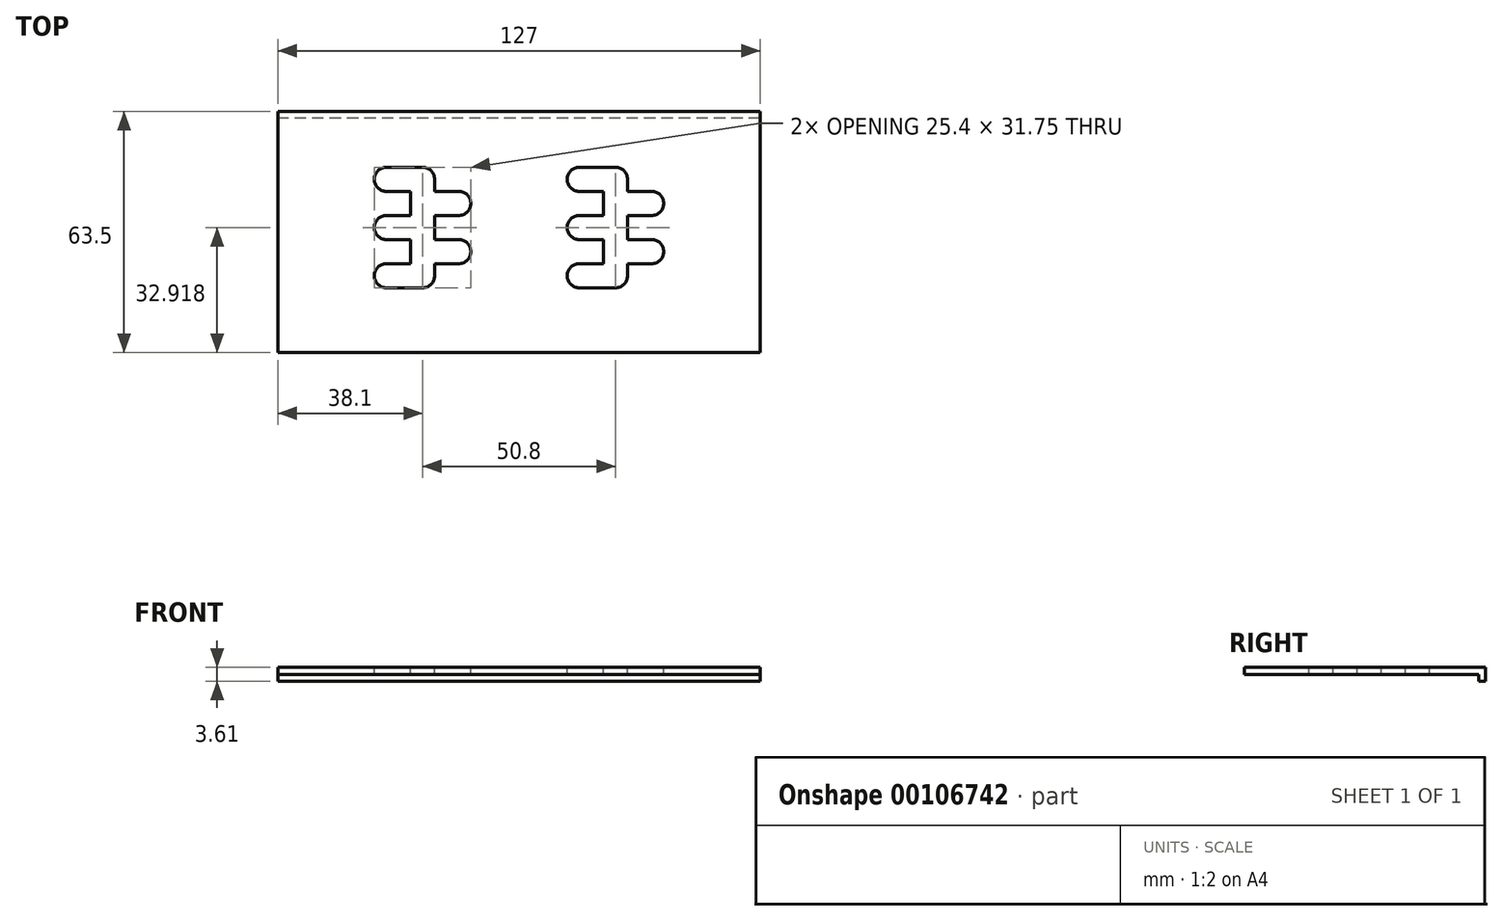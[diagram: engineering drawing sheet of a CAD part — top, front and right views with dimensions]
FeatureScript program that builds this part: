
annotation { "Feature Type Name" : "Feature", "Feature Type Description" : "" }
export const myFeature = defineFeature(function(context is Context, id is Id, definition is map)
    precondition{}
    {
        {
            var Q0;
            Q0=qCreatedBy(makeId("Right.planeOp"),FACE);
            var sketch = newSketch(context, id + "F0", { "sketchPlane" : qUnion([Q0])});
            skLineSegment(sketch, "E0.bottom", {"start": v(29.95, -0.9) * mm, "end": v(-31.75, -0.9) * mm});
            skLineSegment(sketch, "E0.top", {"start": v(31.75, 0.9) * mm, "end": v(-31.75, 0.9) * mm});
            skLineSegment(sketch, "E0.left", {"start": v(31.75, -0.9) * mm, "end": v(31.75, 0.9) * mm});
            skLineSegment(sketch, "E0.right", {"start": v(-31.75, -0.9) * mm, "end": v(-31.75, 0.9) * mm});
            skPoint(sketch, "E0.middle", {"position": v(0, 0) * mm});
            skLineSegment(sketch, "E1", {"start": v(31.75, -0.9) * mm, "end": v(31.75, -2.7) * mm});
            skLineSegment(sketch, "E2", {"start": v(31.75, -2.7) * mm, "end": v(29.95, -2.7) * mm});
            skLineSegment(sketch, "E3", {"start": v(29.95, -2.7) * mm, "end": v(29.95, -0.9) * mm});
            skSolve(sketch);
        }
        {
            var Q0;
            Q0=makeQuery(id+"F0.imprint","IMPRINT",FACE,{"disambiguationData":[TD([[makeQuery(id+"F0.imprint","IMPRINT",EDGE,{"derivedFrom":sQuery(id+"F0.wireOp",EDGE,"E0.bottom")}),-1.0]])]});
            extrude(context, id + "F1", {"entities" : qUnion([Q0]), "depth" : 63.5 * mm, "hasSecondDirection" : true, "secondDirectionOppositeDirection" : true, "secondDirectionDepth" : 63.5 * mm});
        }
        {
            var Q0;
            Q0=makeQuery(id+"F1.opExtrude","SWEPT_FACE",FACE,{"disambiguationData":[OSD([sQuery(id+"F0.wireOp",EDGE,"E0.top")])]});
            var sketch = newSketch(context, id + "F2", { "sketchPlane" : qUnion([Q0])});
            skLineSegment(sketch, "E4", {"start": v(0, 0) * mm, "end": v(-25.4, 0) * mm, "construction": true});
            skLineSegment(sketch, "E5", {"start": v(-38.1, 13.87) * mm, "end": v(-25.4, 13.87) * mm, "construction": true});
            skLineSegment(sketch, "E6", {"start": v(-25.4, 13.87) * mm, "end": v(-25.4, -11.53) * mm, "construction": true});
            skLineSegment(sketch, "E7", {"start": v(-38.1, -11.53) * mm, "end": v(-25.4, -11.53) * mm, "construction": true});
            skLineSegment(sketch, "E8", {"start": v(-25.4, 1.17) * mm, "end": v(-38.1, 1.17) * mm, "construction": true});
            skLineSegment(sketch, "E9", {"start": v(-25.4, 7.52) * mm, "end": v(-12.7, 7.52) * mm, "construction": true});
            skLineSegment(sketch, "E10", {"start": v(-25.4, -5.18) * mm, "end": v(-12.7, -5.18) * mm, "construction": true});
            skLineSegment(sketch, "E11", {"start": v(-38.1, 13.87) * mm, "end": v(-38.1, 13.87) * mm});
            skLineSegment(sketch, "E12", {"start": v(-34.93, 17.04) * mm, "end": v(-25.4, 17.04) * mm});
            skLineSegment(sketch, "E13", {"start": v(-12.7, 7.52) * mm, "end": v(-12.7, 7.52) * mm});
            skLineSegment(sketch, "E14", {"start": v(-22.23, 13.87) * mm, "end": v(-22.23, 10.7) * mm});
            skLineSegment(sketch, "E15", {"start": v(-15.88, 10.7) * mm, "end": v(-22.23, 10.7) * mm});
            skLineSegment(sketch, "E16", {"start": v(-15.88, 4.34) * mm, "end": v(-22.23, 4.34) * mm});
            skLineSegment(sketch, "E17", {"start": v(-22.23, 4.34) * mm, "end": v(-22.23, -2) * mm});
            skLineSegment(sketch, "E18", {"start": v(-12.7, -5.18) * mm, "end": v(-12.7, -5.18) * mm});
            skLineSegment(sketch, "E19", {"start": v(-15.88, -2) * mm, "end": v(-22.23, -2) * mm});
            skLineSegment(sketch, "E20", {"start": v(-15.88, -8.36) * mm, "end": v(-22.23, -8.36) * mm});
            skLineSegment(sketch, "E21", {"start": v(-22.23, -8.36) * mm, "end": v(-22.23, -11.53) * mm});
            skLineSegment(sketch, "E22", {"start": v(-25.4, -14.7) * mm, "end": v(-34.93, -14.7) * mm});
            skLineSegment(sketch, "E23", {"start": v(-38.1, -11.53) * mm, "end": v(-38.1, -11.53) * mm});
            skLineSegment(sketch, "E24", {"start": v(-34.93, -8.36) * mm, "end": v(-28.58, -8.36) * mm});
            skLineSegment(sketch, "E25", {"start": v(-28.58, -8.36) * mm, "end": v(-28.58, -2) * mm});
            skLineSegment(sketch, "E26", {"start": v(-28.58, -2) * mm, "end": v(-34.93, -2) * mm});
            skLineSegment(sketch, "E27", {"start": v(-38.1, 1.17) * mm, "end": v(-38.1, 1.17) * mm});
            skLineSegment(sketch, "E28", {"start": v(-34.93, 10.7) * mm, "end": v(-28.58, 10.7) * mm});
            skLineSegment(sketch, "E29", {"start": v(-28.58, 10.7) * mm, "end": v(-28.58, 4.34) * mm});
            skLineSegment(sketch, "E30", {"start": v(-28.58, 4.34) * mm, "end": v(-34.93, 4.34) * mm});
            skPoint(sketch, "E31.visualSharp", {"position": v(-38.1, 17.04) * mm});
            skArc(sketch, "E31.filletArc", {"start": v(-34.93, 17.04) * mm, "mid": v(-37.17, 16.11) * mm, "end": v(-38.1, 13.87) * mm});
            skPoint(sketch, "E32.visualSharp", {"position": v(-38.1, 10.7) * mm});
            skArc(sketch, "E32.filletArc", {"start": v(-38.1, 13.87) * mm, "mid": v(-37.17, 11.62) * mm, "end": v(-34.93, 10.7) * mm});
            skPoint(sketch, "E33.visualSharp", {"position": v(-22.23, 17.04) * mm});
            skArc(sketch, "E33.filletArc", {"start": v(-22.23, 13.87) * mm, "mid": v(-23.15, 16.11) * mm, "end": v(-25.4, 17.04) * mm});
            skPoint(sketch, "E34.visualSharp", {"position": v(-38.1, 4.34) * mm});
            skArc(sketch, "E34.filletArc", {"start": v(-34.93, 4.34) * mm, "mid": v(-37.17, 3.41) * mm, "end": v(-38.1, 1.17) * mm});
            skPoint(sketch, "E35.visualSharp", {"position": v(-38.1, -2) * mm});
            skArc(sketch, "E35.filletArc", {"start": v(-38.1, 1.17) * mm, "mid": v(-37.17, -1.08) * mm, "end": v(-34.93, -2) * mm});
            skPoint(sketch, "E36.visualSharp", {"position": v(-12.7, 10.7) * mm});
            skArc(sketch, "E36.filletArc", {"start": v(-12.7, 7.52) * mm, "mid": v(-13.63, 9.76) * mm, "end": v(-15.88, 10.7) * mm});
            skPoint(sketch, "E37.visualSharp", {"position": v(-12.7, 4.34) * mm});
            skArc(sketch, "E37.filletArc", {"start": v(-15.88, 4.34) * mm, "mid": v(-13.63, 5.27) * mm, "end": v(-12.7, 7.52) * mm});
            skPoint(sketch, "E38.visualSharp", {"position": v(-12.7, -2) * mm});
            skArc(sketch, "E38.filletArc", {"start": v(-12.7, -5.18) * mm, "mid": v(-13.63, -2.94) * mm, "end": v(-15.88, -2) * mm});
            skPoint(sketch, "E39.visualSharp", {"position": v(-12.7, -8.36) * mm});
            skArc(sketch, "E39.filletArc", {"start": v(-15.88, -8.36) * mm, "mid": v(-13.63, -7.43) * mm, "end": v(-12.7, -5.18) * mm});
            skPoint(sketch, "E40.visualSharp", {"position": v(-22.23, -14.7) * mm});
            skArc(sketch, "E40.filletArc", {"start": v(-25.4, -14.7) * mm, "mid": v(-23.15, -13.78) * mm, "end": v(-22.23, -11.53) * mm});
            skPoint(sketch, "E41.visualSharp", {"position": v(-38.1, -8.36) * mm});
            skArc(sketch, "E41.filletArc", {"start": v(-34.93, -8.36) * mm, "mid": v(-37.17, -9.29) * mm, "end": v(-38.1, -11.53) * mm});
            skPoint(sketch, "E42.visualSharp", {"position": v(-38.1, -14.7) * mm});
            skArc(sketch, "E42.filletArc", {"start": v(-38.1, -11.53) * mm, "mid": v(-37.17, -13.78) * mm, "end": v(-34.93, -14.7) * mm});
            skSolve(sketch);
        }
        {
            var Q0;
            Q0=qSketchRegion(id+"F2",true);
            extrude(context, id + "F3", {"entities" : qUnion([Q0]), "operationType" : NewBodyOperationType.REMOVE, "endBound" : BoundingType.THROUGH_ALL, "oppositeDirection" : true, "depth" : 25.4 * mm});
        }
        {
            var Q0;
            Q0=makeQuery(id+"F1.opExtrude","SWEPT_FACE",FACE,{"disambiguationData":[OSD([sQuery(id+"F0.wireOp",EDGE,"E0.top")])]});
            var sketch = newSketch(context, id + "F4", { "sketchPlane" : qUnion([Q0])});
            skLineSegment(sketch, "E43", {"start": v(55.32, 0.86) * mm, "end": v(29.92, 0.86) * mm, "construction": true});
            skLineSegment(sketch, "E44", {"start": v(12.7, 13.87) * mm, "end": v(25.4, 13.87) * mm, "construction": true});
            skLineSegment(sketch, "E45", {"start": v(25.4, 13.87) * mm, "end": v(25.4, -11.53) * mm, "construction": true});
            skLineSegment(sketch, "E46", {"start": v(12.7, -11.53) * mm, "end": v(25.4, -11.53) * mm, "construction": true});
            skLineSegment(sketch, "E47", {"start": v(25.4, 1.17) * mm, "end": v(12.7, 1.17) * mm, "construction": true});
            skLineSegment(sketch, "E48", {"start": v(25.4, 7.52) * mm, "end": v(38.1, 7.52) * mm, "construction": true});
            skLineSegment(sketch, "E49", {"start": v(25.4, -5.18) * mm, "end": v(38.1, -5.18) * mm, "construction": true});
            skLineSegment(sketch, "E50", {"start": v(12.7, 13.87) * mm, "end": v(12.7, 13.87) * mm});
            skLineSegment(sketch, "E51", {"start": v(15.88, 17.04) * mm, "end": v(25.4, 17.04) * mm});
            skLineSegment(sketch, "E52", {"start": v(38.1, 7.52) * mm, "end": v(38.1, 7.52) * mm});
            skLineSegment(sketch, "E53", {"start": v(28.58, 13.87) * mm, "end": v(28.58, 10.7) * mm});
            skLineSegment(sketch, "E54", {"start": v(34.93, 10.7) * mm, "end": v(28.58, 10.7) * mm});
            skLineSegment(sketch, "E55", {"start": v(34.93, 4.34) * mm, "end": v(28.58, 4.34) * mm});
            skLineSegment(sketch, "E56", {"start": v(28.58, 4.34) * mm, "end": v(28.58, -2) * mm});
            skLineSegment(sketch, "E57", {"start": v(38.1, -5.18) * mm, "end": v(38.1, -5.18) * mm});
            skLineSegment(sketch, "E58", {"start": v(34.93, -2) * mm, "end": v(28.58, -2) * mm});
            skLineSegment(sketch, "E59", {"start": v(34.93, -8.36) * mm, "end": v(28.58, -8.36) * mm});
            skLineSegment(sketch, "E60", {"start": v(28.58, -8.36) * mm, "end": v(28.58, -11.53) * mm});
            skLineSegment(sketch, "E61", {"start": v(25.4, -14.7) * mm, "end": v(15.88, -14.7) * mm});
            skLineSegment(sketch, "E62", {"start": v(12.7, -11.53) * mm, "end": v(12.7, -11.53) * mm});
            skLineSegment(sketch, "E63", {"start": v(15.88, -8.36) * mm, "end": v(22.23, -8.36) * mm});
            skLineSegment(sketch, "E64", {"start": v(22.23, -8.36) * mm, "end": v(22.23, -2) * mm});
            skLineSegment(sketch, "E65", {"start": v(22.23, -2) * mm, "end": v(15.88, -2) * mm});
            skLineSegment(sketch, "E66", {"start": v(12.7, 1.17) * mm, "end": v(12.7, 1.17) * mm});
            skLineSegment(sketch, "E67", {"start": v(15.88, 10.7) * mm, "end": v(22.23, 10.7) * mm});
            skLineSegment(sketch, "E68", {"start": v(22.23, 10.7) * mm, "end": v(22.23, 4.34) * mm});
            skLineSegment(sketch, "E69", {"start": v(22.23, 4.34) * mm, "end": v(15.88, 4.34) * mm});
            skPoint(sketch, "E70.visualSharp", {"position": v(12.7, 17.04) * mm});
            skArc(sketch, "E70.filletArc", {"start": v(15.88, 17.04) * mm, "mid": v(13.63, 16.11) * mm, "end": v(12.7, 13.87) * mm});
            skPoint(sketch, "E71.visualSharp", {"position": v(28.58, 17.04) * mm});
            skArc(sketch, "E71.filletArc", {"start": v(28.58, 13.87) * mm, "mid": v(27.65, 16.11) * mm, "end": v(25.4, 17.04) * mm});
            skPoint(sketch, "E72.visualSharp", {"position": v(12.7, 10.7) * mm});
            skArc(sketch, "E72.filletArc", {"start": v(12.7, 13.87) * mm, "mid": v(13.63, 11.62) * mm, "end": v(15.88, 10.7) * mm});
            skPoint(sketch, "E73.visualSharp", {"position": v(38.1, 10.7) * mm});
            skArc(sketch, "E73.filletArc", {"start": v(38.1, 7.52) * mm, "mid": v(37.17, 9.76) * mm, "end": v(34.93, 10.7) * mm});
            skPoint(sketch, "E74.visualSharp", {"position": v(38.1, 4.34) * mm});
            skArc(sketch, "E74.filletArc", {"start": v(34.93, 4.34) * mm, "mid": v(37.17, 5.27) * mm, "end": v(38.1, 7.52) * mm});
            skPoint(sketch, "E75.visualSharp", {"position": v(12.7, 4.34) * mm});
            skArc(sketch, "E75.filletArc", {"start": v(15.88, 4.34) * mm, "mid": v(13.63, 3.41) * mm, "end": v(12.7, 1.17) * mm});
            skPoint(sketch, "E76.visualSharp", {"position": v(12.7, -2) * mm});
            skArc(sketch, "E76.filletArc", {"start": v(12.7, 1.17) * mm, "mid": v(13.63, -1.08) * mm, "end": v(15.88, -2) * mm});
            skPoint(sketch, "E77.visualSharp", {"position": v(38.1, -2) * mm});
            skArc(sketch, "E77.filletArc", {"start": v(38.1, -5.18) * mm, "mid": v(37.17, -2.94) * mm, "end": v(34.93, -2) * mm});
            skPoint(sketch, "E78.visualSharp", {"position": v(38.1, -8.36) * mm});
            skArc(sketch, "E78.filletArc", {"start": v(34.93, -8.36) * mm, "mid": v(37.17, -7.43) * mm, "end": v(38.1, -5.18) * mm});
            skPoint(sketch, "E79.visualSharp", {"position": v(12.7, -8.36) * mm});
            skArc(sketch, "E79.filletArc", {"start": v(15.88, -8.36) * mm, "mid": v(13.63, -9.29) * mm, "end": v(12.7, -11.53) * mm});
            skPoint(sketch, "E80.visualSharp", {"position": v(12.7, -14.7) * mm});
            skArc(sketch, "E80.filletArc", {"start": v(12.7, -11.53) * mm, "mid": v(13.63, -13.78) * mm, "end": v(15.88, -14.7) * mm});
            skPoint(sketch, "E81.visualSharp", {"position": v(28.58, -14.7) * mm});
            skArc(sketch, "E81.filletArc", {"start": v(25.4, -14.7) * mm, "mid": v(27.65, -13.78) * mm, "end": v(28.58, -11.53) * mm});
            skSolve(sketch);
        }
        {
            var Q0;
            Q0=qSketchRegion(id+"F4",true);
            extrude(context, id + "F5", {"entities" : qUnion([Q0]), "operationType" : NewBodyOperationType.REMOVE, "endBound" : BoundingType.THROUGH_ALL, "oppositeDirection" : true, "depth" : 25.4 * mm});
        }
    });
